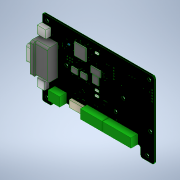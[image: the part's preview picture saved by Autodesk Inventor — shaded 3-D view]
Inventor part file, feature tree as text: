
AUTODESK INVENTOR PART (.ipt)
format: ipt  version: 2020 (Build 240168000, 168)  size: 1,202,688 bytes
history: native  units: in
note: dims shown in document units (in); Inventor stores cm internally (conversion verified against a paired STEP export)
features: extrude x21, other x19, sketch x4, fillet x1
ambient origin geometry x8: Origin, YZ Plane, XZ Plane, XY Plane, X Axis, Y Axis, Z Axis, Center Point
bodies: Solid1 (feature_tree)
feature tree (45):
  other  "Steering.brd"
  extrude  "Steering.brd_Outline"  Depth=0.063in
  extrude  "D2_2"  Depth=0.0394in TaperAngle=0.0deg
  extrude  "D3_4"  Depth=0.0394in TaperAngle=0.0deg
  extrude  "D4_6"  Depth=0.0984in TaperAngle=0.0deg
  extrude  "D7_8"  Depth=0.4921in TaperAngle=0.0deg
  extrude  "J1_10"  Depth=0.2756in TaperAngle=0.0deg
  extrude  "J3_12"  Depth=0.2756in TaperAngle=0.0deg
  extrude  "J4_14"  Depth=0.2756in TaperAngle=0.0deg
  extrude  "J5_16"  Depth=0.1969in TaperAngle=0.0deg
  extrude  "J6_18"  Depth=0.0394in TaperAngle=0.0deg
  extrude  "J7_20"  Depth=0.0394in TaperAngle=0.0deg
  extrude  "J8_22"  Depth=0.0394in TaperAngle=0.0deg
  extrude  "MC1_24"  Depth=0.0394in TaperAngle=0.0deg
  extrude  "S1_26"  Depth=0.0394in TaperAngle=0.0deg
  extrude  "U_3_28"  Depth=0.5118in
  extrude  "U1_30"  Depth=0.0787in TaperAngle=0.0deg
  extrude  "U2_32"  Depth=0.315in
  extrude  "Extrusion18"  Depth=0.6496in
  extrude  "Extrusion19"  Depth=0.1969in
  fillet  "Fillet1"  Radius=0.2461in
  extrude  "Hole Fixing"  Depth=0.0787in
  extrude  "Extrusion21"  Depth=0.2362in TaperAngle=0.0deg
  sketch  "Sketch1"  dims[d0=0.063in d1=0.0in d2=0.063in]
  other  "KINGBRIGHT_LED, LED_AA3528VRVCS_A_1"
  other  "KINGBRIGHT_LED, LED_AA3528VRVCS_A_3"
  other  "KINGBRIGHT_LED, PINK_5"
  other  "CHIP-LED0603, BLUE_7"
  other  "UX60-MB-5S8, UX60-MB-5S8_9"
  other  "MOLEX_5025850670, MOLEX_5025850670_11"
  other  "NONASSMANN_VGA_CONNECTOR, NONASSMANN_VGA_CONNECTOR_13"
  other  "SCREW_TERMINAL_PCB_CONN_8_POLE, PCB_SCREW_TERM_8_15"
  other  "SCREW_TERMINAL_PCB_CONN_6_POLE, PCB_SCREW_TERM_6_17"
  other  "SCREW_TERMINAL_PCB_CONN_3_POLE, PCB_SCREW_TERM_3_19"
  other  "B2PS-CENTERED, B2PS-VH_LF__SN__21"
  other  "TQFP44, ATMEGA32U4-AU_23"
  other  "CTS_DIP_SWITCH, CTS_SWITCH_SPST_25"
  other  "PTS645, PTS645_27"
  other  "TSSOP14, CD4066BPWR_29"
  other  "TSSOP14, CD4066BPWR_31"
  other  "Image1"
  sketch  "Sketch18"  dims[d3=0.0394in d4=0.0in d5=0.0394in d6=0.0in]
  sketch  "Sketch19"  dims[d7=0.0394in d8=0.0in d9=0.0394in d10=0.0in]
  other  "Patchwork_Repair"
  sketch  "Sketch21"  dims[d11=0.1969in d12=0.0in d13=0.0984in d14=0.0in d15=0.4921in d16=0.0in d17=0.2756in d18=0.0in d19=0.2756in d20=0.0in d21=0.2756in d22=0.0in d23=0.1969in d24=0.0in d25=0.0394in d26=0.0in d27=0.0394in d28=0.0in d29=0.0394in d30=0.0in d31=0.0394in d32=0.0in d33=0.0394in d34=0.0in d42=0.5118in d43=0.0787in d44=0.0in d45=0.315in d46=0.6496in d47=0.6135in d48=0.2461in d49=0.0787in d50=0.2362in d51=0.0in d52=0.0787in d54=1.7323in d55=0.3543in d56=0.0181in d57=2.246in d58=0.1969in d59=0.0in d60=0.1299in d61=0.1299in d62=1.1024in d63=1.1024in d64=1.4173in d65=2.9921in d66=0.0in d67=0.0in d68=0.3937in d69=0.7677in d70=0.1299in d71=0.2756in d72=0.1969in]
